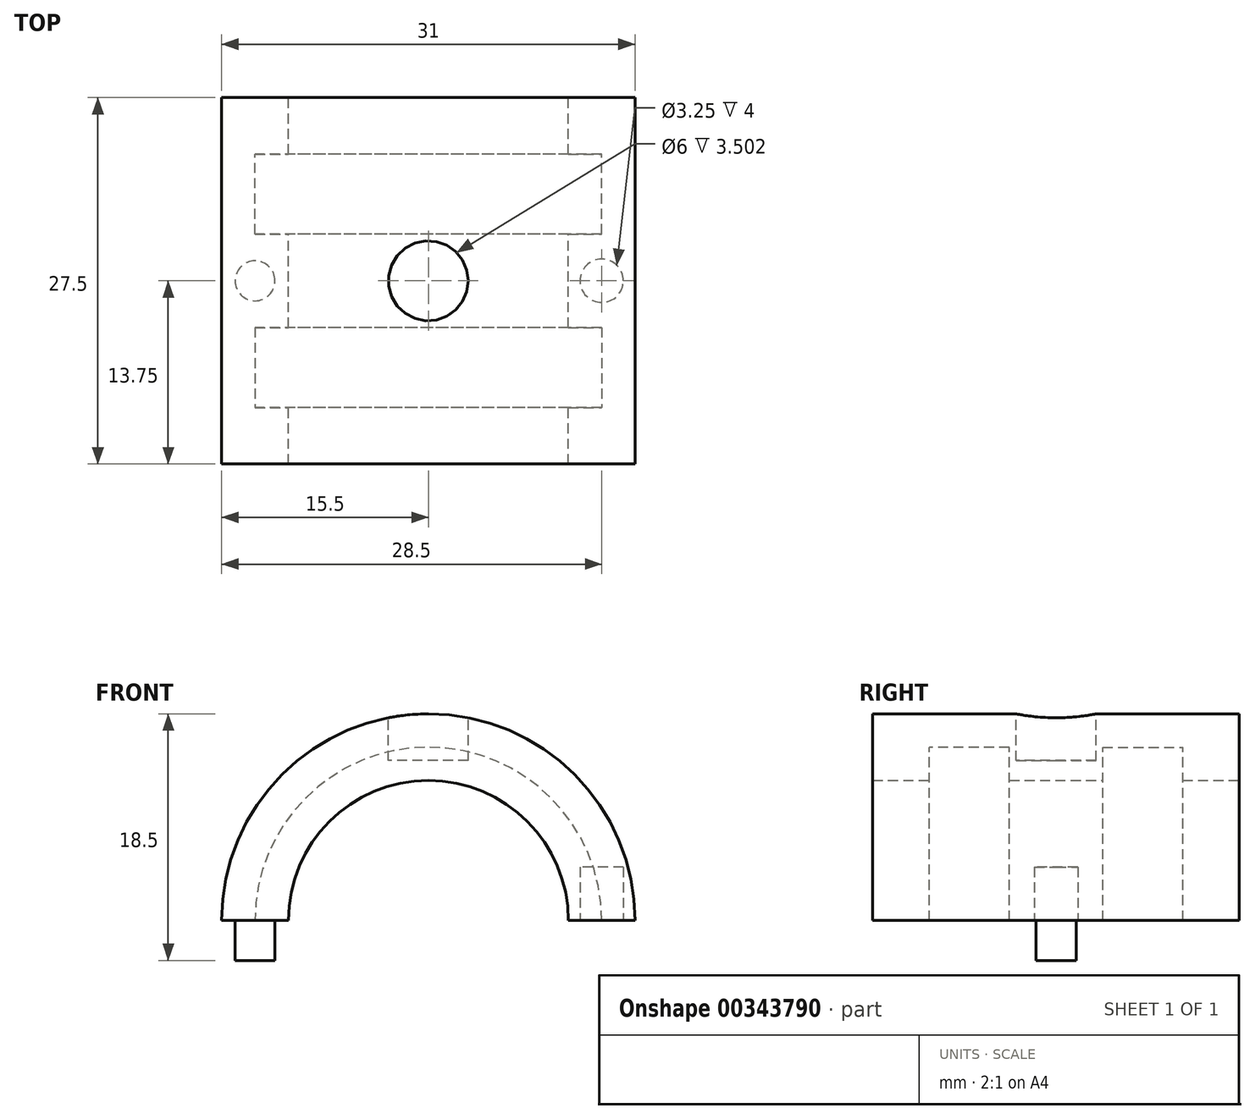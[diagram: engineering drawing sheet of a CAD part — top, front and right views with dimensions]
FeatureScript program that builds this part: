
annotation { "Feature Type Name" : "Feature", "Feature Type Description" : "" }
export const myFeature = defineFeature(function(context is Context, id is Id, definition is map)
    precondition{}
    {
        {
            var Q0;
            Q0=qCreatedBy(makeId("Front.planeOp"),FACE);
            var sketch = newSketch(context, id + "F0", { "sketchPlane" : qUnion([Q0])});
            skArc(sketch, "E0", {"start": v(10.5, 0) * mm, "mid": v(0, 10.5) * mm, "end": v(-10.5, 0) * mm});
            skArc(sketch, "E1", {"start": v(15.5, 0) * mm, "mid": v(0, 15.5) * mm, "end": v(-15.5, 0) * mm});
            skLineSegment(sketch, "E2", {"start": v(-15.5, 0) * mm, "end": v(-10.5, 0) * mm});
            skLineSegment(sketch, "E3", {"start": v(10.5, 0) * mm, "end": v(15.5, 0) * mm});
            skSolve(sketch);
        }
        {
            var Q0;
            {var subQ0=sQuery(id+"F0.wireOp",EDGE,"E1");Q0=makeQuery(id+"F0.imprint","IMPRINT",FACE,{"disambiguationData":[TD([[makeQuery(id+"F0.imprint","IMPRINT",EDGE,{"derivedFrom":subQ0}),1.0]])]});}
            var Q1;
            {var subQ0=sQuery(id+"F0.wireOp",EDGE,"E0");Q1=makeQuery(id+"F0.imprint","IMPRINT",FACE,{"disambiguationData":[TD([[makeQuery(id+"F0.imprint","IMPRINT",EDGE,{"derivedFrom":subQ0}),-1.0]])]});}
            extrude(context, id + "F1", {"entities" : qUnion([Q0, Q1]), "depth" : 27.5 * mm, "offsetDistance" : 25 * mm, "symmetric" : true});
        }
        {
            var Q0;
            Q0=qCreatedBy(makeId("Front.planeOp"),FACE);
            var sketch = newSketch(context, id + "F2", { "sketchPlane" : qUnion([Q0])});
            skSolve(sketch);
        }
        {
            var Q0;
            Q0=qCreatedBy(makeId("Top.planeOp"),FACE);
            var sketch = newSketch(context, id + "F3", { "sketchPlane" : qUnion([Q0])});
            skCircle(sketch, "E4", {"center": v(-13, 0) * mm, "radius": 1.5 * mm});
            skCircle(sketch, "E5", {"center": v(13, 0) * mm, "radius": 1.63 * mm});
            skSolve(sketch);
        }
        {
            var Q0;
            Q0=makeQuery(id+"F3.imprint","IMPRINT",FACE,{"disambiguationData":[TD([[makeQuery(id+"F3.imprint","IMPRINT",EDGE,{"derivedFrom":sQuery(id+"F3.wireOp",EDGE,"E4")}),1.0]])]});
            extrude(context, id + "F4", {"entities" : qUnion([Q0]), "operationType" : NewBodyOperationType.ADD, "oppositeDirection" : true, "depth" : 3 * mm, "offsetDistance" : 25 * mm});
        }
        {
            var Q0;
            Q0=makeQuery(id+"F3.imprint","IMPRINT",FACE,{"disambiguationData":[TD([[makeQuery(id+"F3.imprint","IMPRINT",EDGE,{"derivedFrom":sQuery(id+"F3.wireOp",EDGE,"E5")}),1.0]])]});
            extrude(context, id + "F5", {"entities" : qUnion([Q0]), "operationType" : NewBodyOperationType.REMOVE, "depth" : 4 * mm, "offsetDistance" : 25 * mm});
        }
        {
            var Q0;
            Q0=qBodyType(qCreatedBy(id+"F2",EDGE),BodyType.WIRE);
            var Q1;
            Q1=qCreatedBy(makeId("Front.planeOp"),FACE);
            cPlane(context, id + "F6", {"entities" : qUnion([Q0, Q1]), "cplaneType" : CPlaneType.OFFSET, "offset" : 6.5 * mm, "width" : 150 * mm, "height" : 150 * mm});
        }
        {
            var Q0;
            Q0=qCreatedBy(id+"F6.planeOp",FACE);
            var sketch = newSketch(context, id + "F7", { "sketchPlane" : qUnion([Q0])});
            skCircle(sketch, "E6", {"center": v(0, 0) * mm, "radius": 13 * mm});
            skCircle(sketch, "E7", {"center": v(0, 0) * mm, "radius": 10.5 * mm});
            skSolve(sketch);
        }
        {
            var Q0;
            Q0=qSketchRegion(id+"F7",true);
            extrude(context, id + "F8", {"entities" : qUnion([Q0]), "operationType" : NewBodyOperationType.REMOVE, "oppositeDirection" : true, "depth" : 6 * mm, "offsetDistance" : 25 * mm, "symmetric" : true});
        }
        {
            var Q0;
            Q0=qCreatedBy(makeId("Front.planeOp"),FACE);
            cPlane(context, id + "F9", {"entities" : qUnion([Q0]), "cplaneType" : CPlaneType.OFFSET, "offset" : 6.5 * mm, "oppositeDirection" : true, "width" : 150 * mm, "height" : 150 * mm});
        }
        {
            var Q0;
            Q0=qCreatedBy(id+"F9.planeOp",FACE);
            var sketch = newSketch(context, id + "F10", { "sketchPlane" : qUnion([Q0])});
            skCircle(sketch, "E8", {"center": v(0, 0) * mm, "radius": 10.5 * mm});
            skCircle(sketch, "E9", {"center": v(0, 0) * mm, "radius": 13 * mm});
            skSolve(sketch);
        }
        {
            var Q0;
            Q0=qSketchRegion(id+"F10",true);
            extrude(context, id + "F11", {"entities" : qUnion([Q0]), "operationType" : NewBodyOperationType.REMOVE, "depth" : 6 * mm, "offsetDistance" : 25 * mm, "symmetric" : true});
        }
        {
            var Q0;
            Q0=qCreatedBy(makeId("Top.planeOp"),FACE);
            cPlane(context, id + "F12", {"entities" : qUnion([Q0]), "cplaneType" : CPlaneType.OFFSET, "offset" : 15.5 * mm, "width" : 150 * mm, "height" : 150 * mm});
        }
        {
            var Q0;
            Q0=qCreatedBy(id+"F12.planeOp",FACE);
            var sketch = newSketch(context, id + "F13", { "sketchPlane" : qUnion([Q0])});
            skCircle(sketch, "E10", {"center": v(0, 0) * mm, "radius": 3 * mm});
            skSolve(sketch);
        }
        {
            var Q0;
            Q0 = qSketchRegion(id + "F13", true);
            extrude(context, id + "F14", {"entities" : qUnion([Q0]), "operationType" : NewBodyOperationType.REMOVE, "oppositeDirection" : true, "depth" : 3.5 * mm, "offsetDistance" : 25 * mm});
        }
    });
